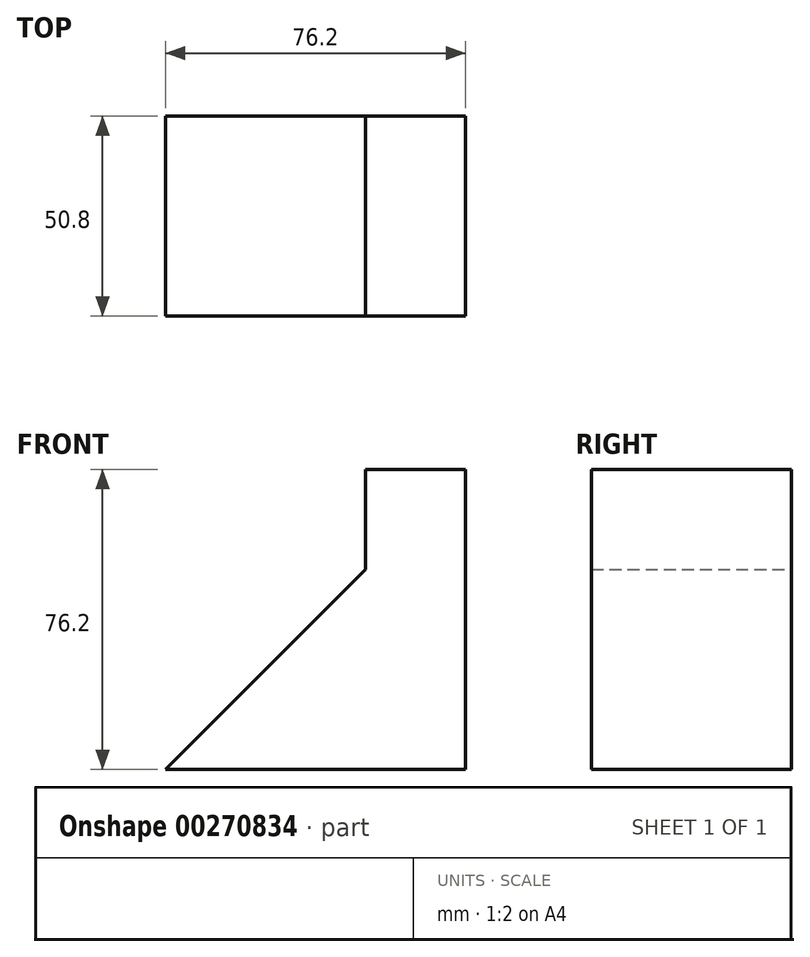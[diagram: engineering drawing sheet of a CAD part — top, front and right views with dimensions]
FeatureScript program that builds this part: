
annotation { "Feature Type Name" : "Feature", "Feature Type Description" : "" }
export const myFeature = defineFeature(function(context is Context, id is Id, definition is map)
    precondition{}
    {
        {
            var Q0;
            Q0=qCreatedBy(makeId("Front.planeOp"),FACE);
            var sketch = newSketch(context, id + "F0", { "sketchPlane" : qUnion([Q0])});
            skLineSegment(sketch, "E0", {"start": v(0, 0) * mm, "end": v(0, 76.2) * mm});
            skLineSegment(sketch, "E1", {"start": v(0, 0) * mm, "end": v(-76.2, 0) * mm});
            skLineSegment(sketch, "E2", {"start": v(0, 76.2) * mm, "end": v(-25.4, 76.2) * mm});
            skLineSegment(sketch, "E3", {"start": v(-25.4, 76.2) * mm, "end": v(-25.4, 50.8) * mm});
            skLineSegment(sketch, "E4", {"start": v(-25.4, 50.8) * mm, "end": v(-76.2, 0) * mm});
            skSolve(sketch);
        }
        {
            var Q0;
            Q0 = qSketchRegion(id + "F0", true);
            extrude(context, id + "F1", {"entities" : qUnion([Q0]), "depth" : 50.8 * mm});
        }
    });
